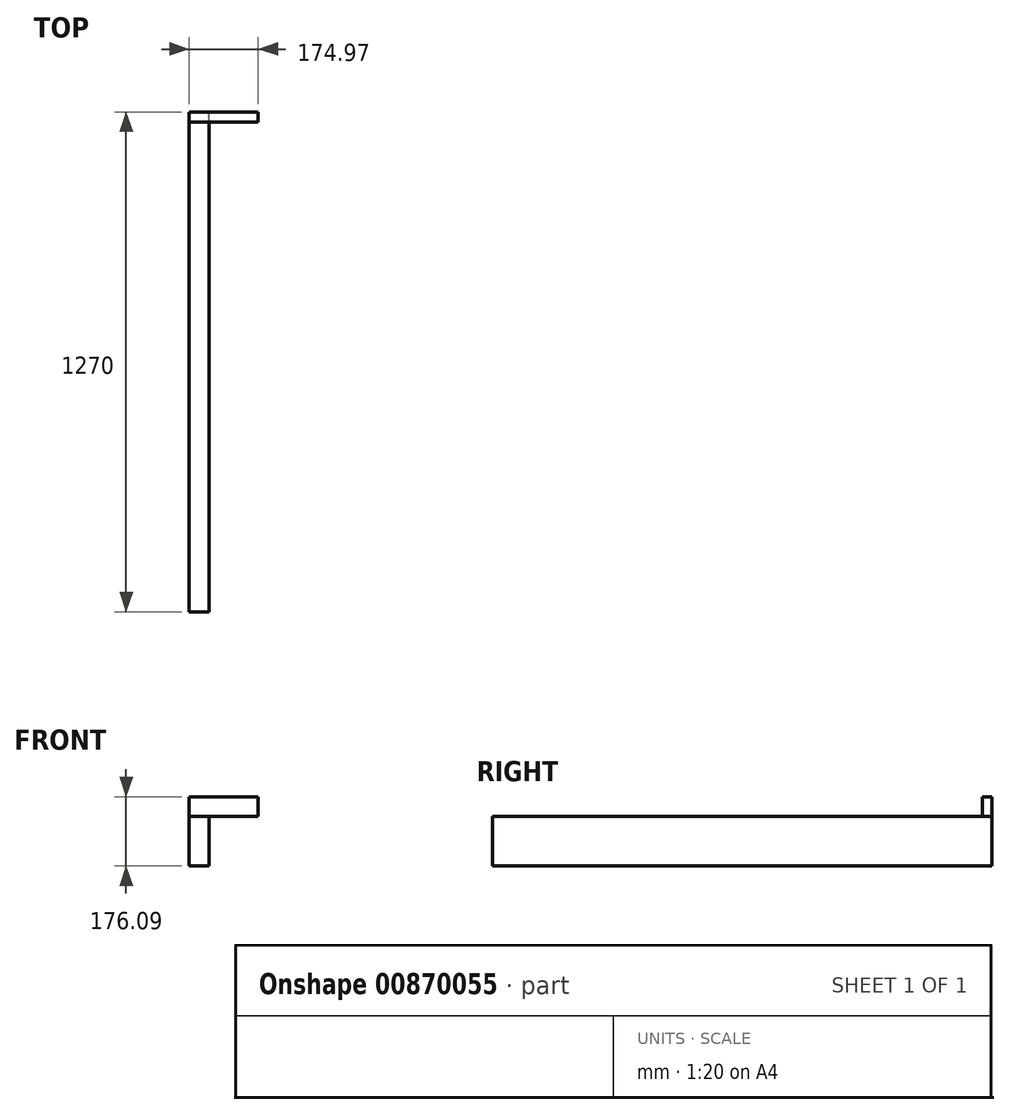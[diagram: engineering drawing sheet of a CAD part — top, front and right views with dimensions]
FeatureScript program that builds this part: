
annotation { "Feature Type Name" : "Feature", "Feature Type Description" : "" }
export const myFeature = defineFeature(function(context is Context, id is Id, definition is map)
    precondition{}
    {
        {
            var Q0;
            Q0=qCreatedBy(makeId("Front.planeOp"),FACE);
            var sketch = newSketch(context, id + "F0", { "sketchPlane" : qUnion([Q0])});
            skLineSegment(sketch, "E0.bottom", {"start": v(0, 0) * mm, "end": v(50.22, 0) * mm});
            skLineSegment(sketch, "E0.top", {"start": v(0, 125.87) * mm, "end": v(50.22, 125.87) * mm});
            skLineSegment(sketch, "E0.left", {"start": v(0, 0) * mm, "end": v(0, 125.87) * mm});
            skLineSegment(sketch, "E0.right", {"start": v(50.22, 0) * mm, "end": v(50.22, 125.87) * mm});
            skLineSegment(sketch, "E1.bottom", {"start": v(50.22, 0) * mm, "end": v(174.97, 0) * mm});
            skLineSegment(sketch, "E1.top", {"start": v(50.22, 64.3) * mm, "end": v(174.97, 64.3) * mm});
            skLineSegment(sketch, "E1.left", {"start": v(50.22, 0) * mm, "end": v(50.22, 64.3) * mm});
            skLineSegment(sketch, "E1.right", {"start": v(174.97, 0) * mm, "end": v(174.97, 64.3) * mm});
            skLineSegment(sketch, "E2.bottom", {"start": v(0, 125.87) * mm, "end": v(174.97, 125.87) * mm});
            skLineSegment(sketch, "E2.top", {"start": v(0, 176.09) * mm, "end": v(174.97, 176.09) * mm});
            skLineSegment(sketch, "E2.left", {"start": v(0, 125.87) * mm, "end": v(0, 176.09) * mm});
            skLineSegment(sketch, "E2.right", {"start": v(174.97, 125.87) * mm, "end": v(174.97, 176.09) * mm});
            skLineSegment(sketch, "E3.bottom", {"start": v(174.97, 176.09) * mm, "end": v(225.18, 176.09) * mm});
            skLineSegment(sketch, "E3.top", {"start": v(174.97, 0) * mm, "end": v(225.18, 0) * mm});
            skLineSegment(sketch, "E3.left", {"start": v(174.97, 176.09) * mm, "end": v(174.97, 0) * mm});
            skLineSegment(sketch, "E3.right", {"start": v(225.18, 176.09) * mm, "end": v(225.18, 0) * mm});
            skLineSegment(sketch, "E4", {"start": v(118.07, 64.3) * mm, "end": v(118.07, 0) * mm});
            skLineSegment(sketch, "E5", {"start": v(118.07, 0) * mm, "end": v(118.07, 5.21) * mm});
            skSolve(sketch);
        }
        {
            var Q0;
            Q0=makeQuery(id+"F0.imprint","IMPRINT",FACE,{"disambiguationData":[TD([[makeQuery(id+"F0.imprint","IMPRINT",EDGE,{"derivedFrom":sQuery(id+"F0.wireOp",EDGE,"E0.bottom")}),1.0]])]});
            extrude(context, id + "F1", {"entities" : qUnion([Q0]), "depth" : 1270 * mm, "offsetDistance" : 25.4 * mm});
        }
        {
            var Q0;
            {var subQ1=sQuery(id+"F0.wireOp",EDGE,"E2.top");Q0=makeQuery(id+"F0.imprint","IMPRINT",FACE,{"disambiguationData":[TD([[makeQuery(id+"F0.imprint","IMPRINT",EDGE,{"derivedFrom":subQ1}),-1.0]])]});}
            extrude(context, id + "F2", {"entities" : qUnion([Q0]), "operationType" : NewBodyOperationType.ADD, "depth" : 25.4 * mm, "offsetDistance" : 25.4 * mm});
        }
    });
